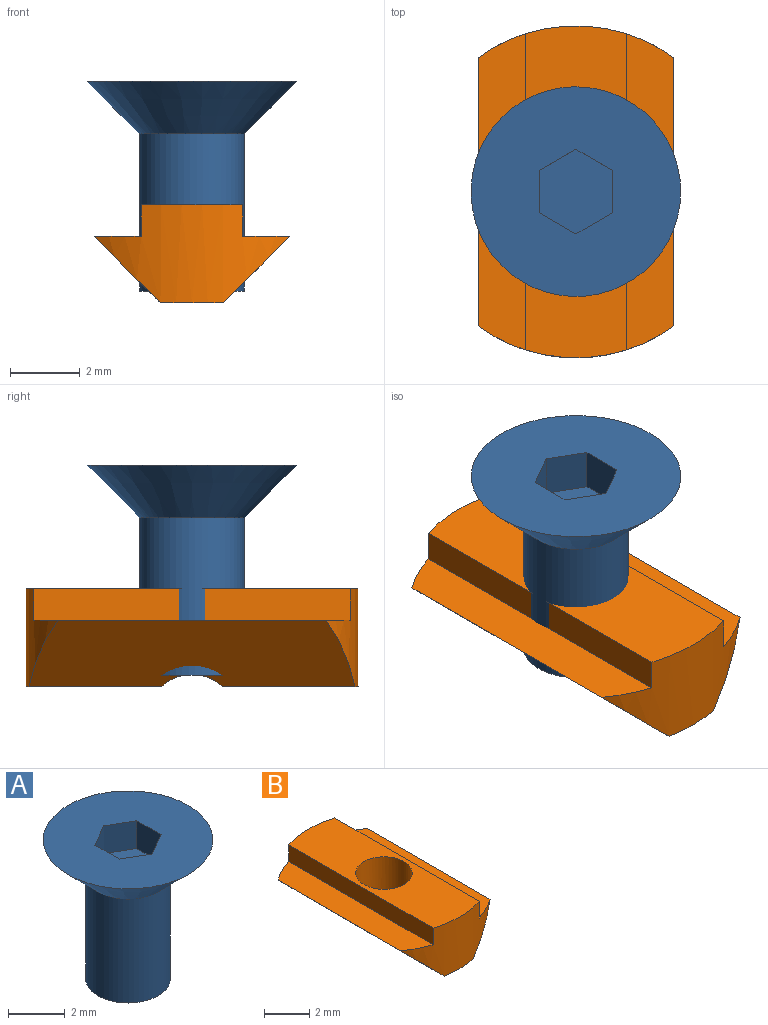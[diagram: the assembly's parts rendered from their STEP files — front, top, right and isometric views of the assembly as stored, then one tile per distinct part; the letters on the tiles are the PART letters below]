
ASSEMBLY  parts=2 mates=1
PART A: 11 faces, bbox 6x6x6 mm
  f0: plane 6x6mm, normal (0,0,1), area 24.5mm2, adj f3,f4,f5,f6,f7,f8,f9
  f1: cylinder r=1.5mm len=4.5mm, axis (0,0,1), area 42.4mm2, adj f2,f3
  f2: plane 3x3mm, normal (0,0,-1), area 7.1mm2, adj f1
  f3: cone r=3mm half-angle=45deg, axis (0,0,1), area 30mm2, adj f0,f1
  f4: plane 1.2x1.05mm, normal (-0.5,-0.87,0), area 1.5mm2, adj f0,f5,f9,f10
  f5: plane 1.2x1.05mm, normal (0.5,-0.87,0), area 1.5mm2, adj f0,f4,f6,f10
  f6: plane 1.21x1.2mm, normal (1,0,0), area 1.5mm2, adj f0,f5,f7,f10
  f7: plane 1.2x1.05mm, normal (0.5,0.87,0), area 1.5mm2, adj f0,f6,f8,f10
  f8: plane 1.2x1.05mm, normal (-0.5,0.87,0), area 1.5mm2, adj f0,f7,f9,f10
  f9: plane 1.21x1.2mm, normal (-1,0,0), area 1.5mm2, adj f0,f4,f8,f10
  f10: plane 2.43x2.1mm, normal (0,0,1), area 3.8mm2, adj f4,f5,f6,f7,f8,f9
PART B: 12 faces, bbox 5.6x9.5x2.8 mm
  f0: plane 3.88x1.8mm, normal (0,0,-1), area 6.5mm2, adj f4,f6,f9,f11
  f1: plane 9.5x2.9mm, normal (0,0,1), area 22.2mm2, adj f2,f8,f9,f10,f11
  f2: plane 9.05x0.9mm, normal (-1,0,0), area 8.1mm2, adj f1,f3,f9,f10
  f3: plane 9.05x1.35mm, normal (0,0,1), area 11.4mm2, adj f2,f4,f9,f10
  f4: plane 9.33x1.9mm, normal (-0.71,0,-0.71), area 22.7mm2, adj f0,f3,f5,f9,f10,f11
  f5: plane 3.88x1.8mm, normal (0,0,-1), area 6.5mm2, adj f4,f6,f10,f11
  f6: plane 9.33x1.9mm, normal (0.71,0,-0.71), area 22.7mm2, adj f0,f5,f7,f9,f10,f11
  f7: plane 9.05x1.35mm, normal (0,0,1), area 11.4mm2, adj f6,f8,f9,f10
  f8: plane 9.05x0.9mm, normal (1,0,0), area 8.1mm2, adj f1,f7,f9,f10
  f9: cylinder r=4.75mm len=5.6mm, axis (0,0,1), area 9.9mm2, adj f0,f1,f2,f3,f4,f6,f7,f8
  f10: cylinder r=4.75mm len=5.6mm, axis (0,0,1), area 9.9mm2, adj f1,f2,f3,f4,f5,f6,f7,f8
  f11: cylinder r=1.25mm len=2.8mm, axis (0,0,1), area 21.1mm2, adj f0,f1,f4,f5,f6
PLACE A t=(0,0,3.53)mm
PLACE B at identity fixed
MATE fastened A.f1 <-> B.f9  axis (0,0,1) through (0,0,2.03)mm
